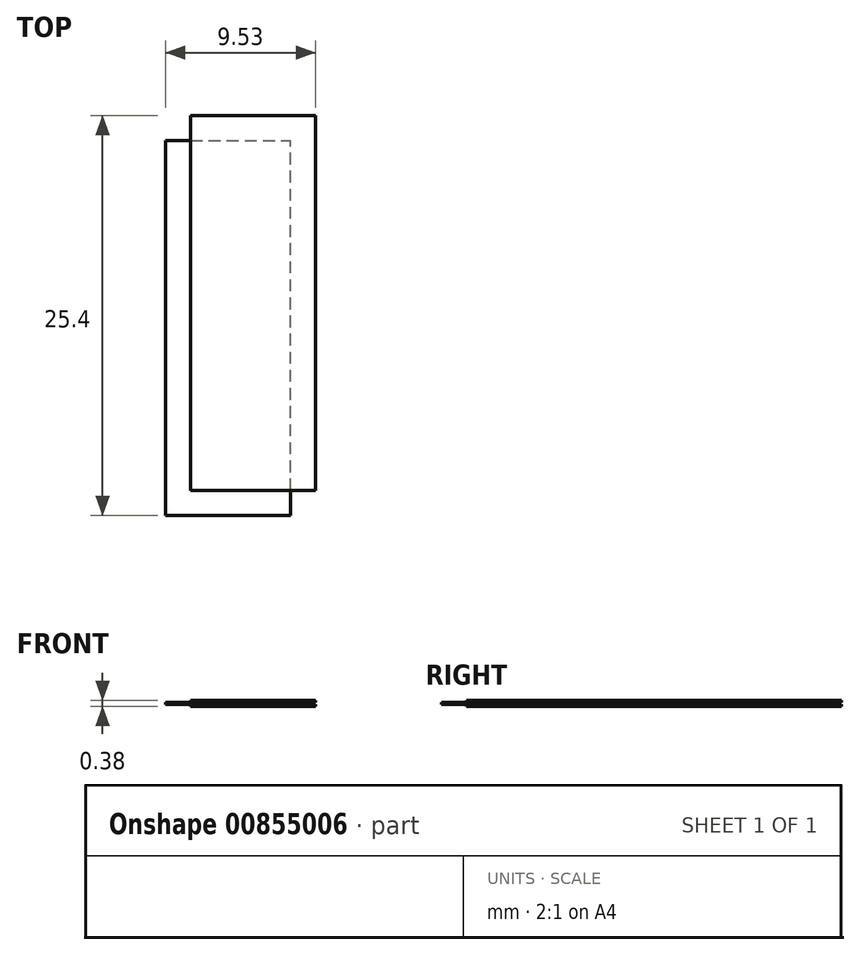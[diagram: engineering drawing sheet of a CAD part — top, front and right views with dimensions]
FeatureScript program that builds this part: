
annotation { "Feature Type Name" : "Feature", "Feature Type Description" : "" }
export const myFeature = defineFeature(function(context is Context, id is Id, definition is map)
    precondition{}
    {
        {
            assignVariable(context, id + "F0", {"name" : "haut", "anyValue" : 3 / 8});
        }
        {
            assignVariable(context, id + "F1", {"name" : "rain_haut", "anyValue" : 1 / 8});
        }
        {
            var Q0;
            Q0=qCreatedBy(makeId("Top.planeOp"),FACE);
            var sketch = newSketch(context, id + "F2", { "sketchPlane" : qUnion([Q0])});
            skLineSegment(sketch, "E0.bottom", {"start": v(0, 0) * mm, "end": v(7.94, 0) * mm});
            skLineSegment(sketch, "E0.top", {"start": v(0, 23.81) * mm, "end": v(7.94, 23.81) * mm});
            skLineSegment(sketch, "E0.left", {"start": v(0, 0) * mm, "end": v(0, 23.81) * mm});
            skLineSegment(sketch, "E0.right", {"start": v(7.94, 0) * mm, "end": v(7.94, 23.81) * mm});
            skSolve(sketch);
        }
        {
            var Q0;
            Q0 = qSketchRegion(id + "F2", true);
            extrude(context, id + "F3", {"entities" : qUnion([Q0]), "depth" : ((getVariable(context, 'haut') - getVariable(context, 'rain_haut')) / 2) * mm, "offsetDistance" : 25.4 * mm});
        }
        {
            var Q0;
            Q0=makeQuery(id+"F3.opExtrude","CAP_FACE",FACE,{"disambiguationData":[OSD([sQuery(id+"F2.wireOp",EDGE,"E0.bottom"),sQuery(id+"F2.wireOp",EDGE,"E0.top"),sQuery(id+"F2.wireOp",EDGE,"E0.left"),sQuery(id+"F2.wireOp",EDGE,"E0.right")])],"isStart":false});
            var sketch = newSketch(context, id + "F4", { "sketchPlane" : qUnion([Q0])});
            skLineSegment(sketch, "E1.bottom", {"start": v(-1.59, -1.59) * mm, "end": v(6.35, -1.59) * mm});
            skLineSegment(sketch, "E1.top", {"start": v(-1.59, 22.23) * mm, "end": v(6.35, 22.23) * mm});
            skLineSegment(sketch, "E1.left", {"start": v(-1.59, -1.59) * mm, "end": v(-1.59, 22.23) * mm});
            skLineSegment(sketch, "E1.right", {"start": v(6.35, -1.59) * mm, "end": v(6.35, 22.23) * mm});
            skSolve(sketch);
        }
        {
            var Q0;
            Q0 = qSketchRegion(id + "F4", true);
            extrude(context, id + "F5", {"entities" : qUnion([Q0]), "operationType" : NewBodyOperationType.ADD, "depth" : (getVariable(context, 'rain_haut')) * mm, "offsetDistance" : 25.4 * mm});
        }
        {
            var Q0;
            Q0=makeQuery(id+"F5.opExtrude","CAP_FACE",FACE,{"disambiguationData":[OSD([sQuery(id+"F4.wireOp",EDGE,"E1.bottom"),sQuery(id+"F4.wireOp",EDGE,"E1.top"),sQuery(id+"F4.wireOp",EDGE,"E1.left"),sQuery(id+"F4.wireOp",EDGE,"E1.right")])],"isStart":false});
            var sketch = newSketch(context, id + "F6", { "sketchPlane" : qUnion([Q0])});
            skLineSegment(sketch, "E2.bottom", {"start": v(0, 0) * mm, "end": v(7.94, 0) * mm});
            skLineSegment(sketch, "E2.top", {"start": v(0, 23.81) * mm, "end": v(7.94, 23.81) * mm});
            skLineSegment(sketch, "E2.left", {"start": v(0, 0) * mm, "end": v(0, 23.81) * mm});
            skLineSegment(sketch, "E2.right", {"start": v(7.94, 0) * mm, "end": v(7.94, 23.81) * mm});
            skSolve(sketch);
        }
        {
            var Q0;
            Q0 = qSketchRegion(id + "F6", true);
            extrude(context, id + "F7", {"entities" : qUnion([Q0]), "operationType" : NewBodyOperationType.ADD, "depth" : ((getVariable(context, 'haut') - getVariable(context, 'rain_haut')) / 2) * mm, "offsetDistance" : 25.4 * mm});
        }
    });
